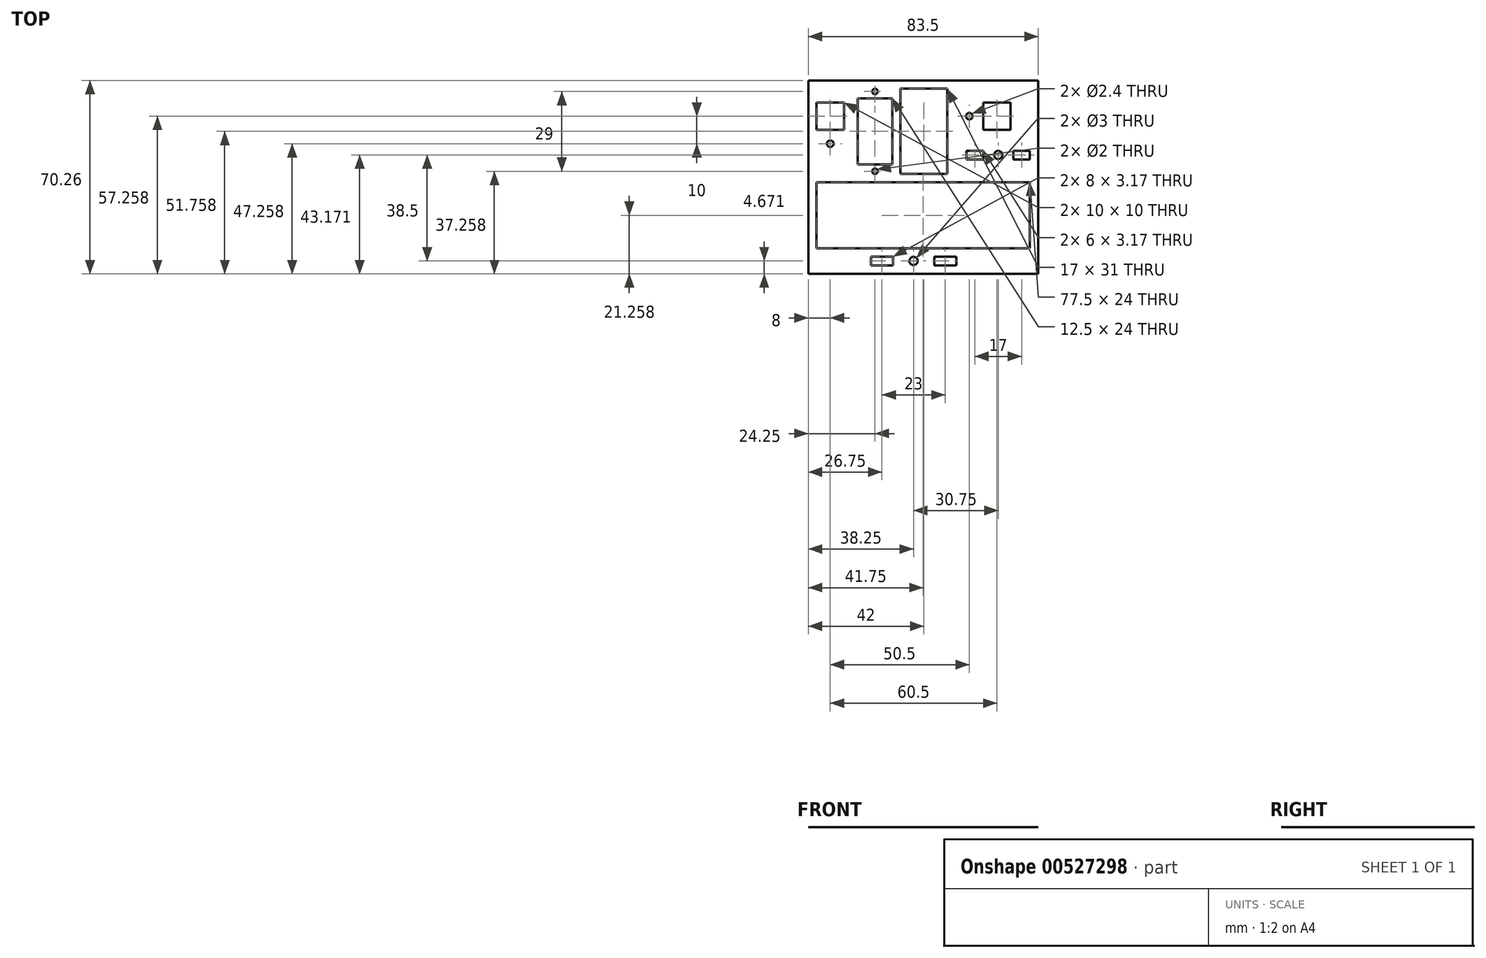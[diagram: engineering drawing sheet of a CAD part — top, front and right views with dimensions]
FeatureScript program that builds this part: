
annotation { "Feature Type Name" : "Feature", "Feature Type Description" : "" }
export const myFeature = defineFeature(function(context is Context, id is Id, definition is map)
    precondition{}
    {
        {
            var Q0;
            Q0=qCreatedBy(makeId("Top.planeOp"),FACE);
            var sketch = newSketch(context, id + "F0", { "sketchPlane" : qUnion([Q0])});
            skLineSegment(sketch, "E0.bottom", {"start": v(-21.23, 55.9) * mm, "end": v(-8.73, 55.9) * mm});
            skLineSegment(sketch, "E0.top", {"start": v(-21.23, 31.9) * mm, "end": v(-8.73, 31.9) * mm});
            skLineSegment(sketch, "E0.left", {"start": v(-21.23, 55.9) * mm, "end": v(-21.23, 31.9) * mm});
            skLineSegment(sketch, "E0.right", {"start": v(-8.73, 55.9) * mm, "end": v(-8.73, 31.9) * mm});
            skPoint(sketch, "E0.middle", {"position": v(-14.98, 43.9) * mm});
            skCircle(sketch, "E1", {"center": v(-14.98, 58.4) * mm, "radius": 1 * mm});
            skLineSegment(sketch, "E2", {"start": v(-14.98, 43.9) * mm, "end": v(-8.73, 43.9) * mm});
            skCircle(sketch, "E3.MirrorC", {"center": v(-14.98, 29.4) * mm, "radius": 1 * mm});
            skLineSegment(sketch, "E4.bottom", {"start": v(-39.23, 62.4) * mm, "end": v(44.27, 62.4) * mm});
            skLineSegment(sketch, "E4.top", {"start": v(-39.23, -7.85) * mm, "end": v(44.27, -7.85) * mm});
            skLineSegment(sketch, "E4.left", {"start": v(-39.23, 62.4) * mm, "end": v(-39.23, -7.85) * mm});
            skLineSegment(sketch, "E4.right", {"start": v(44.27, 62.4) * mm, "end": v(44.27, -7.85) * mm});
            skCircle(sketch, "E5", {"center": v(-0.98, -3.18) * mm, "radius": 1.5 * mm});
            skLineSegment(sketch, "E6.bottom", {"start": v(6.52, -1.6) * mm, "end": v(14.52, -1.6) * mm});
            skLineSegment(sketch, "E6.top", {"start": v(6.52, -4.77) * mm, "end": v(14.52, -4.77) * mm});
            skLineSegment(sketch, "E6.left", {"start": v(6.52, -1.6) * mm, "end": v(6.52, -4.77) * mm});
            skLineSegment(sketch, "E6.right", {"start": v(14.52, -1.6) * mm, "end": v(14.52, -4.77) * mm});
            skPoint(sketch, "E6.middle", {"position": v(10.52, -3.18) * mm});
            skLineSegment(sketch, "E7", {"start": v(-0.98, -3.18) * mm, "end": v(-0.98, -4.68) * mm});
            skLineSegment(sketch, "E8.MirrorCS", {"start": v(-8.48, -1.6) * mm, "end": v(-8.48, -4.77) * mm});
            skLineSegment(sketch, "E9.MirrorCS", {"start": v(-8.48, -1.6) * mm, "end": v(-16.48, -1.6) * mm});
            skLineSegment(sketch, "E10.MirrorCS", {"start": v(-16.48, -1.6) * mm, "end": v(-16.48, -4.77) * mm});
            skLineSegment(sketch, "E11.MirrorCS", {"start": v(-8.48, -4.77) * mm, "end": v(-16.48, -4.77) * mm});
            skLineSegment(sketch, "E12.bottom", {"start": v(-36.23, 44.4) * mm, "end": v(-26.23, 44.4) * mm});
            skLineSegment(sketch, "E12.top", {"start": v(-36.23, 34.4) * mm, "end": v(-26.23, 34.4) * mm});
            skLineSegment(sketch, "E12.left", {"start": v(-36.23, 44.4) * mm, "end": v(-36.23, 34.4) * mm});
            skLineSegment(sketch, "E12.right", {"start": v(-26.23, 44.4) * mm, "end": v(-26.23, 34.4) * mm});
            skPoint(sketch, "E12.middle", {"position": v(-31.23, 39.4) * mm});
            skLineSegment(sketch, "E13.top", {"start": v(-36.23, 54.4) * mm, "end": v(-26.23, 54.4) * mm});
            skLineSegment(sketch, "E13.left", {"start": v(-36.23, 44.4) * mm, "end": v(-36.23, 54.4) * mm});
            skLineSegment(sketch, "E13.right", {"start": v(-26.23, 44.4) * mm, "end": v(-26.23, 54.4) * mm});
            skCircle(sketch, "E14", {"center": v(-31.23, 39.4) * mm, "radius": 1.2 * mm});
            skCircle(sketch, "E15", {"center": v(29.77, 35.32) * mm, "radius": 1.5 * mm});
            skLineSegment(sketch, "E16.bottom", {"start": v(18.27, 36.9) * mm, "end": v(24.27, 36.9) * mm});
            skLineSegment(sketch, "E16.top", {"start": v(18.27, 33.73) * mm, "end": v(24.27, 33.73) * mm});
            skLineSegment(sketch, "E16.left", {"start": v(18.27, 36.9) * mm, "end": v(18.27, 33.73) * mm});
            skLineSegment(sketch, "E16.right", {"start": v(24.27, 36.9) * mm, "end": v(24.27, 33.73) * mm});
            skPoint(sketch, "E16.middle", {"position": v(21.27, 35.32) * mm});
            skLineSegment(sketch, "E17", {"start": v(29.77, 35.32) * mm, "end": v(29.77, 33.82) * mm});
            skLineSegment(sketch, "E18.MirrorCS", {"start": v(35.27, 36.9) * mm, "end": v(35.27, 33.73) * mm});
            skLineSegment(sketch, "E19.MirrorCS", {"start": v(41.27, 36.9) * mm, "end": v(35.27, 36.9) * mm});
            skLineSegment(sketch, "E20.MirrorCS", {"start": v(41.27, 36.9) * mm, "end": v(41.27, 33.73) * mm});
            skLineSegment(sketch, "E21.MirrorCS", {"start": v(41.27, 33.73) * mm, "end": v(35.27, 33.73) * mm});
            skLineSegment(sketch, "E22.bottom", {"start": v(24.27, 54.4) * mm, "end": v(34.27, 54.4) * mm});
            skLineSegment(sketch, "E22.top", {"start": v(24.27, 44.4) * mm, "end": v(34.27, 44.4) * mm});
            skLineSegment(sketch, "E22.left", {"start": v(24.27, 54.4) * mm, "end": v(24.27, 44.4) * mm});
            skLineSegment(sketch, "E22.right", {"start": v(34.27, 54.4) * mm, "end": v(34.27, 44.4) * mm});
            skLineSegment(sketch, "E23.bottom", {"start": v(24.27, 44.4) * mm, "end": v(14.27, 44.4) * mm});
            skLineSegment(sketch, "E23.top", {"start": v(24.27, 54.4) * mm, "end": v(14.27, 54.4) * mm});
            skLineSegment(sketch, "E23.left", {"start": v(24.27, 44.4) * mm, "end": v(24.27, 54.4) * mm});
            skLineSegment(sketch, "E23.right", {"start": v(14.27, 44.4) * mm, "end": v(14.27, 54.4) * mm});
            skCircle(sketch, "E24", {"center": v(19.27, 49.4) * mm, "radius": 1.2 * mm});
            skPoint(sketch, "E24.centerSnap0", {"position": v(24.27, 49.4) * mm});
            skPoint(sketch, "E24.centerSnap1", {"position": v(19.27, 54.4) * mm});
            skLineSegment(sketch, "E25.bottom", {"start": v(41.27, 25.4) * mm, "end": v(-36.23, 25.4) * mm});
            skLineSegment(sketch, "E25.top", {"start": v(41.27, 1.4) * mm, "end": v(-36.23, 1.4) * mm});
            skLineSegment(sketch, "E25.left", {"start": v(41.27, 25.4) * mm, "end": v(41.27, 1.4) * mm});
            skLineSegment(sketch, "E25.right", {"start": v(-36.23, 25.4) * mm, "end": v(-36.23, 1.4) * mm});
            skLineSegment(sketch, "E26.bottom", {"start": v(11.27, 59.4) * mm, "end": v(-5.73, 59.4) * mm});
            skLineSegment(sketch, "E26.top", {"start": v(11.27, 28.4) * mm, "end": v(-5.73, 28.4) * mm});
            skLineSegment(sketch, "E26.left", {"start": v(11.27, 59.4) * mm, "end": v(11.27, 28.4) * mm});
            skLineSegment(sketch, "E26.right", {"start": v(-5.73, 59.4) * mm, "end": v(-5.73, 28.4) * mm});
            skSolve(sketch);
        }
        {
            var Q0;
            {var subQ3=sQuery(id+"F0.wireOp",EDGE,"E0.bottom");Q0=makeQuery(id+"F0.imprint","IMPRINT",FACE,{"disambiguationData":[TD([[makeQuery(id+"F0.imprint","IMPRINT",EDGE,{"derivedFrom":subQ3}),1.0]])]});}
            var Q1;
            Q1=makeQuery(id+"F0.imprint","IMPRINT",FACE,{"disambiguationData":[TD([[makeQuery(id+"F0.imprint","IMPRINT",EDGE,{"derivedFrom":sQuery(id+"F0.wireOp",EDGE,"E12.top")}),1.0]])]});
            var Q2;
            Q2=makeQuery(id+"F0.imprint","IMPRINT",FACE,{"disambiguationData":[TD([[makeQuery(id+"F0.imprint","IMPRINT",EDGE,{"derivedFrom":sQuery(id+"F0.wireOp",EDGE,"acsabYuh-lohw-pKPj-6WYc-orZH53f84UEU.top")}),1.0]])]});
            var Q3;
            Q3=makeQuery(id+"F0.imprint","IMPRINT",FACE,{"disambiguationData":[TD([[makeQuery(id+"F0.imprint","IMPRINT",EDGE,{"derivedFrom":sQuery(id+"F0.wireOp",EDGE,"E23.bottom")}),-1.0]])]});
            var Q4;
            {var subQ1=sQuery(id+"F0.wireOp",EDGE,"E25.bottom");var subQ3=sQuery(id+"F0.wireOp",EDGE,"jaePNMbD-eRRB-ghYV-nGq6-sAyCAhomSmL6");var subQ4=makeQuery(id+"F0.imprint","INTERSECT",VERTEX,{"derivedFrom":[subQ1,subQ3]});Q4=makeQuery(id+"F0.imprint","IMPRINT",FACE,{"disambiguationData":[TD([[makeQuery(id+"F0.imprint","IMPRINT",EDGE,{"disambiguationData":[TD([[subQ4,-1.0]])],"derivedFrom":subQ3}),-1.0]])]});}
            var Q5;
            {var subQ1=sQuery(id+"F0.wireOp",EDGE,"E25.right");var subQ3=sQuery(id+"F0.wireOp",EDGE,"pwMugsL7-Pr4C-R3Zh-KxXD-xpTdDHvJqvbZ");var subQ4=makeQuery(id+"F0.imprint","INTERSECT",VERTEX,{"derivedFrom":[subQ1,subQ3]});Q5=makeQuery(id+"F0.imprint","IMPRINT",FACE,{"disambiguationData":[TD([[makeQuery(id+"F0.imprint","IMPRINT",EDGE,{"disambiguationData":[TD([[subQ4,-1.0]])],"derivedFrom":subQ3}),1.0]])]});}
            var Q6;
            {var subQ0=sQuery(id+"F0.wireOp",EDGE,"7ldsxbgT-gCQ7-0gYQ-SICk-B76UX7BRpSP7");var subQ5=sQuery(id+"F0.wireOp",EDGE,"jaePNMbD-eRRB-ghYV-nGq6-sAyCAhomSmL6");var subQ6=makeQuery(id+"F0.imprint","INTERSECT",VERTEX,{"derivedFrom":[subQ0,subQ5]});Q6=makeQuery(id+"F0.imprint","IMPRINT",FACE,{"disambiguationData":[TD([[makeQuery(id+"F0.imprint","IMPRINT",EDGE,{"disambiguationData":[TD([[subQ6,1.0]])],"derivedFrom":subQ5}),1.0]])]});}
            var Q7;
            {var subQ0=sQuery(id+"F0.wireOp",EDGE,"7ldsxbgT-gCQ7-0gYQ-SICk-B76UX7BRpSP7");var subQ5=sQuery(id+"F0.wireOp",EDGE,"jaePNMbD-eRRB-ghYV-nGq6-sAyCAhomSmL6");var subQ6=makeQuery(id+"F0.imprint","INTERSECT",VERTEX,{"derivedFrom":[subQ0,subQ5]});Q7=makeQuery(id+"F0.imprint","IMPRINT",FACE,{"disambiguationData":[TD([[makeQuery(id+"F0.imprint","IMPRINT",EDGE,{"disambiguationData":[TD([[subQ6,-1.0]])],"derivedFrom":subQ5}),1.0]])]});}
            var Q8;
            {var subQ1=sQuery(id+"F0.wireOp",EDGE,"E25.left");var subQ3=sQuery(id+"F0.wireOp",EDGE,"jaePNMbD-eRRB-ghYV-nGq6-sAyCAhomSmL6");var subQ4=makeQuery(id+"F0.imprint","INTERSECT",VERTEX,{"derivedFrom":[subQ1,subQ3]});Q8=makeQuery(id+"F0.imprint","IMPRINT",FACE,{"disambiguationData":[TD([[makeQuery(id+"F0.imprint","IMPRINT",EDGE,{"disambiguationData":[TD([[subQ4,1.0]])],"derivedFrom":subQ3}),-1.0]])]});}
            var Q9;
            {var subQ1=sQuery(id+"F0.wireOp",EDGE,"E25.top");var subQ3=sQuery(id+"F0.wireOp",EDGE,"pwMugsL7-Pr4C-R3Zh-KxXD-xpTdDHvJqvbZ");var subQ4=makeQuery(id+"F0.imprint","INTERSECT",VERTEX,{"derivedFrom":[subQ1,subQ3]});Q9=makeQuery(id+"F0.imprint","IMPRINT",FACE,{"disambiguationData":[TD([[makeQuery(id+"F0.imprint","IMPRINT",EDGE,{"disambiguationData":[TD([[subQ4,1.0]])],"derivedFrom":subQ3}),1.0]])]});}
            var Q10;
            {var subQ0=sQuery(id+"F0.wireOp",EDGE,"7ldsxbgT-gCQ7-0gYQ-SICk-B76UX7BRpSP7");var subQ5=sQuery(id+"F0.wireOp",EDGE,"pwMugsL7-Pr4C-R3Zh-KxXD-xpTdDHvJqvbZ");var subQ6=makeQuery(id+"F0.imprint","INTERSECT",VERTEX,{"derivedFrom":[subQ0,subQ5]});Q10=makeQuery(id+"F0.imprint","IMPRINT",FACE,{"disambiguationData":[TD([[makeQuery(id+"F0.imprint","IMPRINT",EDGE,{"disambiguationData":[TD([[subQ6,-1.0]])],"derivedFrom":subQ5}),-1.0]])]});}
            var Q11;
            {var subQ0=sQuery(id+"F0.wireOp",EDGE,"7ldsxbgT-gCQ7-0gYQ-SICk-B76UX7BRpSP7");var subQ5=sQuery(id+"F0.wireOp",EDGE,"pwMugsL7-Pr4C-R3Zh-KxXD-xpTdDHvJqvbZ");var subQ6=makeQuery(id+"F0.imprint","INTERSECT",VERTEX,{"derivedFrom":[subQ0,subQ5]});Q11=makeQuery(id+"F0.imprint","IMPRINT",FACE,{"disambiguationData":[TD([[makeQuery(id+"F0.imprint","IMPRINT",EDGE,{"disambiguationData":[TD([[subQ6,1.0]])],"derivedFrom":subQ5}),-1.0]])]});}
            var Q12;
            {var subQ0=sQuery(id+"F0.wireOp",EDGE,"EnQ4RziA-duUB-NQTJ-yLjv-mI0L0BYuHflg");var subQ1=sQuery(id+"F0.wireOp",EDGE,"Pe9INAYW-GEdB-20Hl-V33A-gMFSaRPhHrGd");var subQ2=makeQuery(id+"F0.imprint","INTERSECT",VERTEX,{"derivedFrom":[subQ1,subQ0]});Q12=makeQuery(id+"F0.imprint","IMPRINT",FACE,{"disambiguationData":[TD([[makeQuery(id+"F0.imprint","IMPRINT",EDGE,{"disambiguationData":[TD([[subQ2,-1.0]])],"derivedFrom":subQ1}),-1.0]])]});}
            var Q13;
            {var subQ0=sQuery(id+"F0.wireOp",EDGE,"EnQ4RziA-duUB-NQTJ-yLjv-mI0L0BYuHflg");var subQ1=sQuery(id+"F0.wireOp",EDGE,"Pe9INAYW-GEdB-20Hl-V33A-gMFSaRPhHrGd");var subQ2=makeQuery(id+"F0.imprint","INTERSECT",VERTEX,{"derivedFrom":[subQ1,subQ0]});Q13=makeQuery(id+"F0.imprint","IMPRINT",FACE,{"disambiguationData":[TD([[makeQuery(id+"F0.imprint","IMPRINT",EDGE,{"disambiguationData":[TD([[subQ2,-1.0]])],"derivedFrom":subQ1}),1.0]])]});}
            var Q14;
            {var subQ0=sQuery(id+"F0.wireOp",EDGE,"7ldsxbgT-gCQ7-0gYQ-SICk-B76UX7BRpSP7");var subQ1=sQuery(id+"F0.wireOp",EDGE,"Pe9INAYW-GEdB-20Hl-V33A-gMFSaRPhHrGd");var subQ2=makeQuery(id+"F0.imprint","INTERSECT",VERTEX,{"derivedFrom":[subQ1,subQ0]});Q14=makeQuery(id+"F0.imprint","IMPRINT",FACE,{"disambiguationData":[TD([[makeQuery(id+"F0.imprint","IMPRINT",EDGE,{"disambiguationData":[TD([[subQ2,-1.0]])],"derivedFrom":subQ1}),1.0]])]});}
            var Q15;
            {var subQ0=sQuery(id+"F0.wireOp",EDGE,"7ldsxbgT-gCQ7-0gYQ-SICk-B76UX7BRpSP7");var subQ1=sQuery(id+"F0.wireOp",EDGE,"Pe9INAYW-GEdB-20Hl-V33A-gMFSaRPhHrGd");var subQ2=makeQuery(id+"F0.imprint","INTERSECT",VERTEX,{"derivedFrom":[subQ1,subQ0]});Q15=makeQuery(id+"F0.imprint","IMPRINT",FACE,{"disambiguationData":[TD([[makeQuery(id+"F0.imprint","IMPRINT",EDGE,{"disambiguationData":[TD([[subQ2,-1.0]])],"derivedFrom":subQ1}),-1.0]])]});}
            extrude(context, id + "F1", {"entities" : qUnion([Q0, Q1, Q2, Q3, Q4, Q5, Q6, Q7, Q8, Q9, Q10, Q11, Q12, Q13, Q14, Q15]), "depth" : 1 / 203.2 * mm, "offsetDistance" : 25 * mm});
        }
    });
